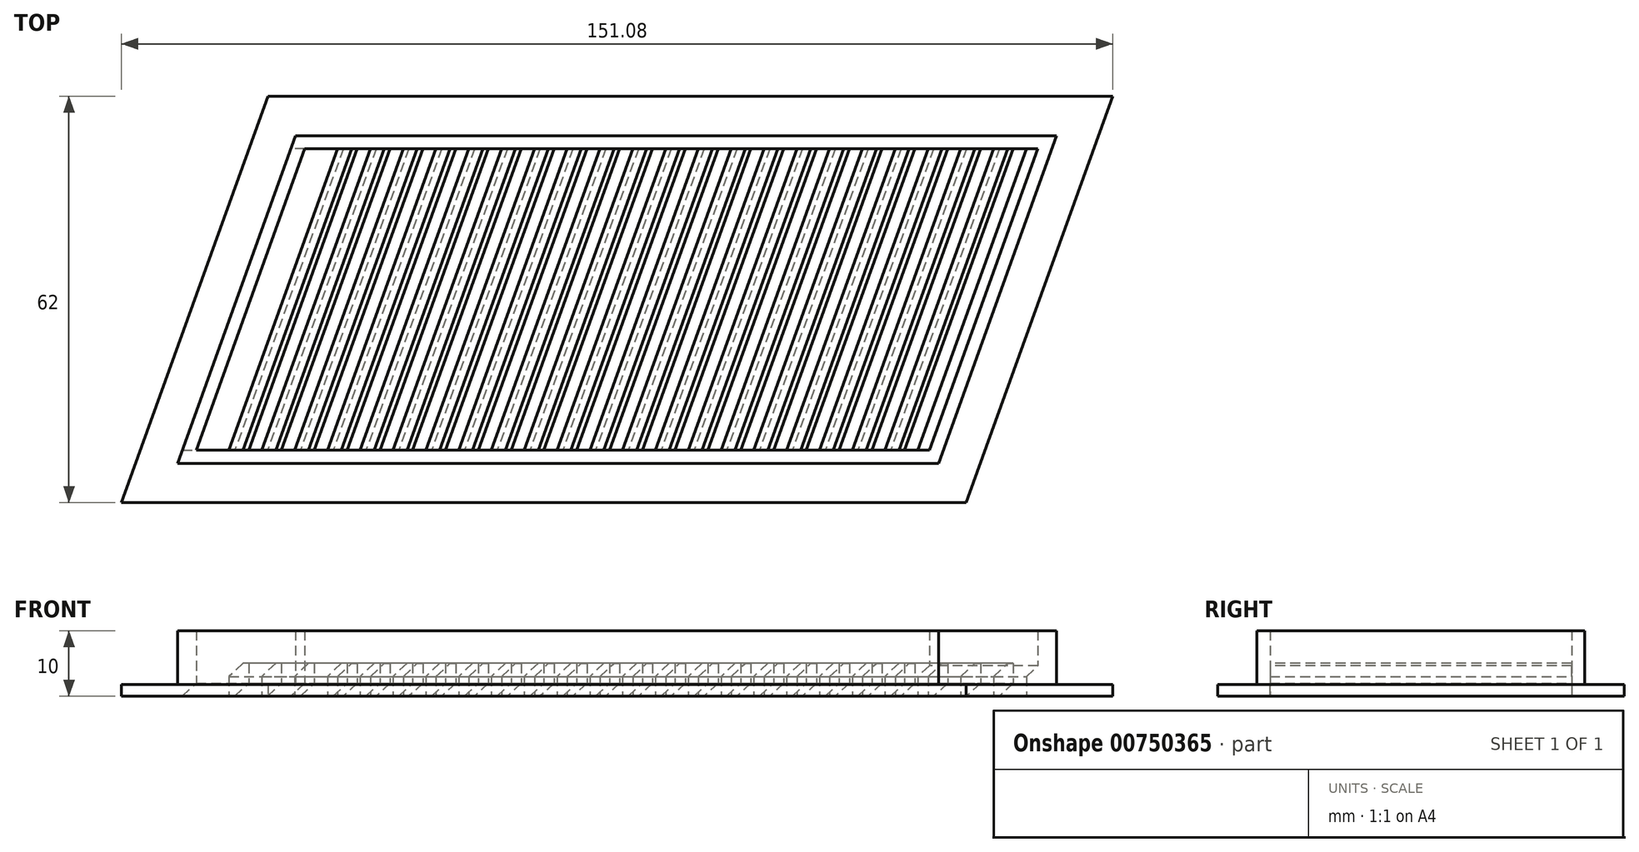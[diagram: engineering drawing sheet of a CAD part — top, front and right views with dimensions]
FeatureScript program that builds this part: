
annotation { "Feature Type Name" : "Feature", "Feature Type Description" : "" }
export const myFeature = defineFeature(function(context is Context, id is Id, definition is map)
    precondition{}
    {
        {
            var Q0;
            Q0=qCreatedBy(makeId("Top.planeOp"),FACE);
            var sketch = newSketch(context, id + "F0", { "sketchPlane" : qUnion([Q0])});
            skLineSegment(sketch, "E0", {"start": v(-116, 0) * mm, "end": v(0, 0) * mm});
            skLineSegment(sketch, "E1", {"start": v(-116, 0) * mm, "end": v(-98, 0) * mm});
            skLineSegment(sketch, "E2", {"start": v(-98, 0) * mm, "end": v(-98, 50) * mm, "construction": true});
            skLineSegment(sketch, "E3", {"start": v(18, 50) * mm, "end": v(-98, 50) * mm});
            skLineSegment(sketch, "E4", {"start": v(-98, 50) * mm, "end": v(-116, 0) * mm});
            skLineSegment(sketch, "E5", {"start": v(18, 50) * mm, "end": v(0, 0) * mm});
            skLineSegment(sketch, "E6.0", {"start": v(26.54, 56) * mm, "end": v(-102.22, 56) * mm});
            skLineSegment(sketch, "E6.1", {"start": v(26.54, 56) * mm, "end": v(4.22, -6) * mm});
            skLineSegment(sketch, "E6.2", {"start": v(-124.54, -6) * mm, "end": v(4.22, -6) * mm});
            skLineSegment(sketch, "E6.3", {"start": v(-102.22, 56) * mm, "end": v(-124.54, -6) * mm});
            skLineSegment(sketch, "E7.0", {"start": v(15.15, 48) * mm, "end": v(-96.6, 48) * mm});
            skLineSegment(sketch, "E7.1", {"start": v(15.15, 48) * mm, "end": v(-1.4, 2) * mm});
            skLineSegment(sketch, "E7.2", {"start": v(-113.15, 2) * mm, "end": v(-1.4, 2) * mm});
            skLineSegment(sketch, "E7.3", {"start": v(-96.6, 48) * mm, "end": v(-113.15, 2) * mm});
            skLineSegment(sketch, "E8.1.0.0", {"start": v(-91.6, 48) * mm, "end": v(-108.15, 2) * mm});
            skLineSegment(sketch, "E8.direction1", {"start": v(-113.15, 2) * mm, "end": v(-108.15, 2) * mm, "construction": true});
            skLineSegment(sketch, "E9.1.0.0", {"start": v(-88.6, 48) * mm, "end": v(-105.15, 2) * mm});
            skLineSegment(sketch, "E9.direction1", {"start": v(-113.15, 2) * mm, "end": v(-105.15, 2) * mm, "construction": true});
            skLineSegment(sketch, "E10.1.0.0", {"start": v(-86.6, 48) * mm, "end": v(-103.15, 2) * mm});
            skLineSegment(sketch, "E10.1.0.1", {"start": v(-83.6, 48) * mm, "end": v(-100.15, 2) * mm});
            skLineSegment(sketch, "E10.2.0.0", {"start": v(-81.6, 48) * mm, "end": v(-98.15, 2) * mm});
            skLineSegment(sketch, "E10.2.0.1", {"start": v(-78.6, 48) * mm, "end": v(-95.15, 2) * mm});
            skLineSegment(sketch, "E10.3.0.0", {"start": v(-76.6, 48) * mm, "end": v(-93.15, 2) * mm});
            skLineSegment(sketch, "E10.3.0.1", {"start": v(-73.6, 48) * mm, "end": v(-90.15, 2) * mm});
            skLineSegment(sketch, "E10.4.0.0", {"start": v(-71.6, 48) * mm, "end": v(-88.15, 2) * mm});
            skLineSegment(sketch, "E10.4.0.1", {"start": v(-68.6, 48) * mm, "end": v(-85.15, 2) * mm});
            skLineSegment(sketch, "E10.5.0.0", {"start": v(-66.6, 48) * mm, "end": v(-83.15, 2) * mm});
            skLineSegment(sketch, "E10.5.0.1", {"start": v(-63.6, 48) * mm, "end": v(-80.15, 2) * mm});
            skLineSegment(sketch, "E10.6.0.0", {"start": v(-61.6, 48) * mm, "end": v(-78.15, 2) * mm});
            skLineSegment(sketch, "E10.6.0.1", {"start": v(-58.6, 48) * mm, "end": v(-75.15, 2) * mm});
            skLineSegment(sketch, "E10.7.0.0", {"start": v(-56.6, 48) * mm, "end": v(-73.15, 2) * mm});
            skLineSegment(sketch, "E10.7.0.1", {"start": v(-53.6, 48) * mm, "end": v(-70.15, 2) * mm});
            skLineSegment(sketch, "E10.8.0.0", {"start": v(-51.6, 48) * mm, "end": v(-68.15, 2) * mm});
            skLineSegment(sketch, "E10.8.0.1", {"start": v(-48.6, 48) * mm, "end": v(-65.15, 2) * mm});
            skLineSegment(sketch, "E10.9.0.0", {"start": v(-46.6, 48) * mm, "end": v(-63.15, 2) * mm});
            skLineSegment(sketch, "E10.9.0.1", {"start": v(-43.6, 48) * mm, "end": v(-60.15, 2) * mm});
            skLineSegment(sketch, "E10.direction1", {"start": v(-108.15, 2) * mm, "end": v(-103.15, 2) * mm, "construction": true});
            skLineSegment(sketch, "E11.0.10.0", {"start": v(-41.6, 48) * mm, "end": v(-58.15, 2) * mm});
            skLineSegment(sketch, "E11.3.10.0", {"start": v(-38.6, 48) * mm, "end": v(-55.15, 2) * mm});
            skLineSegment(sketch, "E11.0.11.0", {"start": v(-36.6, 48) * mm, "end": v(-53.15, 2) * mm});
            skLineSegment(sketch, "E11.3.11.0", {"start": v(-33.6, 48) * mm, "end": v(-50.15, 2) * mm});
            skLineSegment(sketch, "E11.0.12.0", {"start": v(-31.6, 48) * mm, "end": v(-48.15, 2) * mm});
            skLineSegment(sketch, "E11.3.12.0", {"start": v(-28.6, 48) * mm, "end": v(-45.15, 2) * mm});
            skLineSegment(sketch, "E11.0.13.0", {"start": v(-26.6, 48) * mm, "end": v(-43.15, 2) * mm});
            skLineSegment(sketch, "E11.3.13.0", {"start": v(-23.6, 48) * mm, "end": v(-40.15, 2) * mm});
            skLineSegment(sketch, "E11.0.14.0", {"start": v(-21.6, 48) * mm, "end": v(-38.15, 2) * mm});
            skLineSegment(sketch, "E11.3.14.0", {"start": v(-18.6, 48) * mm, "end": v(-35.15, 2) * mm});
            skLineSegment(sketch, "E11.0.15.0", {"start": v(-16.6, 48) * mm, "end": v(-33.15, 2) * mm});
            skLineSegment(sketch, "E11.3.15.0", {"start": v(-13.6, 48) * mm, "end": v(-30.15, 2) * mm});
            skLineSegment(sketch, "E11.0.16.0", {"start": v(-11.6, 48) * mm, "end": v(-28.15, 2) * mm});
            skLineSegment(sketch, "E11.3.16.0", {"start": v(-8.6, 48) * mm, "end": v(-25.15, 2) * mm});
            skLineSegment(sketch, "E11.0.17.0", {"start": v(-6.6, 48) * mm, "end": v(-23.15, 2) * mm});
            skLineSegment(sketch, "E11.3.17.0", {"start": v(-3.6, 48) * mm, "end": v(-20.15, 2) * mm});
            skLineSegment(sketch, "E11.0.18.0", {"start": v(-1.6, 48) * mm, "end": v(-18.15, 2) * mm});
            skLineSegment(sketch, "E11.3.18.0", {"start": v(1.4, 48) * mm, "end": v(-15.15, 2) * mm});
            skLineSegment(sketch, "E11.0.19.0", {"start": v(3.4, 48) * mm, "end": v(-13.15, 2) * mm});
            skLineSegment(sketch, "E11.3.19.0", {"start": v(6.4, 48) * mm, "end": v(-10.15, 2) * mm});
            skLineSegment(sketch, "E12.0.20.0", {"start": v(8.4, 48) * mm, "end": v(-8.15, 2) * mm});
            skLineSegment(sketch, "E12.3.20.0", {"start": v(11.4, 48) * mm, "end": v(-5.15, 2) * mm});
            skLineSegment(sketch, "E12.0.21.0", {"start": v(13.4, 48) * mm, "end": v(-3.15, 2) * mm});
            skSolve(sketch);
        }
        {
            var Q0;
            Q0=makeQuery(id+"F0.imprint","IMPRINT",FACE,{"disambiguationData":[TD([[makeQuery(id+"F0.imprint","IMPRINT",EDGE,{"derivedFrom":sQuery(id+"F0.wireOp",EDGE,"E0")}),-1.0]])]});
            var Q1;
            Q1 = qConstructionFilter(qBodyType(qCreatedBy(id + "F0" ,EDGE), BodyType.WIRE), ConstructionObject.NO);
            extrude(context, id + "F1", {"entities" : qUnion([Q0]), "surfaceEntities" : qUnion([Q1]), "depth" : 1.8 * mm, "offsetDistance" : 25 * mm});
        }
        {
            var Q0;
            Q0=makeQuery(id+"F0.imprint","IMPRINT",FACE,{"disambiguationData":[TD([[makeQuery(id+"F0.imprint","IMPRINT",EDGE,{"derivedFrom":sQuery(id+"F0.wireOp",EDGE,"E0")}),1.0]])]});
            var Q1;
            {var subQ0=sQuery(id+"F0.wireOp",EDGE,"E8.1.0.0");Q1=makeQuery(id+"F0.imprint","IMPRINT",FACE,{"disambiguationData":[TD([[makeQuery(id+"F0.imprint","IMPRINT",EDGE,{"derivedFrom":subQ0}),1.0]])]});}
            var Q2;
            {var subQ0=sQuery(id+"F0.wireOp",EDGE,"E10.1.0.0");Q2=makeQuery(id+"F0.imprint","IMPRINT",FACE,{"disambiguationData":[TD([[makeQuery(id+"F0.imprint","IMPRINT",EDGE,{"derivedFrom":subQ0}),1.0]])]});}
            var Q3;
            {var subQ0=sQuery(id+"F0.wireOp",EDGE,"E10.2.0.0");Q3=makeQuery(id+"F0.imprint","IMPRINT",FACE,{"disambiguationData":[TD([[makeQuery(id+"F0.imprint","IMPRINT",EDGE,{"derivedFrom":subQ0}),1.0]])]});}
            var Q4;
            {var subQ0=sQuery(id+"F0.wireOp",EDGE,"E10.3.0.0");Q4=makeQuery(id+"F0.imprint","IMPRINT",FACE,{"disambiguationData":[TD([[makeQuery(id+"F0.imprint","IMPRINT",EDGE,{"derivedFrom":subQ0}),1.0]])]});}
            var Q5;
            {var subQ0=sQuery(id+"F0.wireOp",EDGE,"E10.4.0.0");Q5=makeQuery(id+"F0.imprint","IMPRINT",FACE,{"disambiguationData":[TD([[makeQuery(id+"F0.imprint","IMPRINT",EDGE,{"derivedFrom":subQ0}),1.0]])]});}
            var Q6;
            {var subQ0=sQuery(id+"F0.wireOp",EDGE,"E10.5.0.0");Q6=makeQuery(id+"F0.imprint","IMPRINT",FACE,{"disambiguationData":[TD([[makeQuery(id+"F0.imprint","IMPRINT",EDGE,{"derivedFrom":subQ0}),1.0]])]});}
            var Q7;
            {var subQ0=sQuery(id+"F0.wireOp",EDGE,"E10.6.0.0");Q7=makeQuery(id+"F0.imprint","IMPRINT",FACE,{"disambiguationData":[TD([[makeQuery(id+"F0.imprint","IMPRINT",EDGE,{"derivedFrom":subQ0}),1.0]])]});}
            var Q8;
            {var subQ0=sQuery(id+"F0.wireOp",EDGE,"E10.7.0.0");Q8=makeQuery(id+"F0.imprint","IMPRINT",FACE,{"disambiguationData":[TD([[makeQuery(id+"F0.imprint","IMPRINT",EDGE,{"derivedFrom":subQ0}),1.0]])]});}
            var Q9;
            {var subQ0=sQuery(id+"F0.wireOp",EDGE,"E10.8.0.0");Q9=makeQuery(id+"F0.imprint","IMPRINT",FACE,{"disambiguationData":[TD([[makeQuery(id+"F0.imprint","IMPRINT",EDGE,{"derivedFrom":subQ0}),1.0]])]});}
            var Q10;
            {var subQ0=sQuery(id+"F0.wireOp",EDGE,"E10.9.0.0");Q10=makeQuery(id+"F0.imprint","IMPRINT",FACE,{"disambiguationData":[TD([[makeQuery(id+"F0.imprint","IMPRINT",EDGE,{"derivedFrom":subQ0}),1.0]])]});}
            var Q11;
            {var subQ0=sQuery(id+"F0.wireOp",EDGE,"E11.0.10.0");Q11=makeQuery(id+"F0.imprint","IMPRINT",FACE,{"disambiguationData":[TD([[makeQuery(id+"F0.imprint","IMPRINT",EDGE,{"derivedFrom":subQ0}),1.0]])]});}
            var Q12;
            {var subQ0=sQuery(id+"F0.wireOp",EDGE,"E11.0.11.0");Q12=makeQuery(id+"F0.imprint","IMPRINT",FACE,{"disambiguationData":[TD([[makeQuery(id+"F0.imprint","IMPRINT",EDGE,{"derivedFrom":subQ0}),1.0]])]});}
            var Q13;
            {var subQ0=sQuery(id+"F0.wireOp",EDGE,"E11.0.12.0");Q13=makeQuery(id+"F0.imprint","IMPRINT",FACE,{"disambiguationData":[TD([[makeQuery(id+"F0.imprint","IMPRINT",EDGE,{"derivedFrom":subQ0}),1.0]])]});}
            var Q14;
            {var subQ0=sQuery(id+"F0.wireOp",EDGE,"E11.0.13.0");Q14=makeQuery(id+"F0.imprint","IMPRINT",FACE,{"disambiguationData":[TD([[makeQuery(id+"F0.imprint","IMPRINT",EDGE,{"derivedFrom":subQ0}),1.0]])]});}
            var Q15;
            {var subQ0=sQuery(id+"F0.wireOp",EDGE,"E11.0.14.0");Q15=makeQuery(id+"F0.imprint","IMPRINT",FACE,{"disambiguationData":[TD([[makeQuery(id+"F0.imprint","IMPRINT",EDGE,{"derivedFrom":subQ0}),1.0]])]});}
            var Q16;
            {var subQ0=sQuery(id+"F0.wireOp",EDGE,"E11.0.15.0");Q16=makeQuery(id+"F0.imprint","IMPRINT",FACE,{"disambiguationData":[TD([[makeQuery(id+"F0.imprint","IMPRINT",EDGE,{"derivedFrom":subQ0}),1.0]])]});}
            var Q17;
            {var subQ0=sQuery(id+"F0.wireOp",EDGE,"E11.0.16.0");Q17=makeQuery(id+"F0.imprint","IMPRINT",FACE,{"disambiguationData":[TD([[makeQuery(id+"F0.imprint","IMPRINT",EDGE,{"derivedFrom":subQ0}),1.0]])]});}
            var Q18;
            {var subQ0=sQuery(id+"F0.wireOp",EDGE,"E11.0.17.0");Q18=makeQuery(id+"F0.imprint","IMPRINT",FACE,{"disambiguationData":[TD([[makeQuery(id+"F0.imprint","IMPRINT",EDGE,{"derivedFrom":subQ0}),1.0]])]});}
            var Q19;
            {var subQ0=sQuery(id+"F0.wireOp",EDGE,"E11.0.18.0");Q19=makeQuery(id+"F0.imprint","IMPRINT",FACE,{"disambiguationData":[TD([[makeQuery(id+"F0.imprint","IMPRINT",EDGE,{"derivedFrom":subQ0}),1.0]])]});}
            var Q20;
            {var subQ0=sQuery(id+"F0.wireOp",EDGE,"E11.0.19.0");Q20=makeQuery(id+"F0.imprint","IMPRINT",FACE,{"disambiguationData":[TD([[makeQuery(id+"F0.imprint","IMPRINT",EDGE,{"derivedFrom":subQ0}),1.0]])]});}
            var Q21;
            {var subQ0=sQuery(id+"F0.wireOp",EDGE,"E12.0.20.0");Q21=makeQuery(id+"F0.imprint","IMPRINT",FACE,{"disambiguationData":[TD([[makeQuery(id+"F0.imprint","IMPRINT",EDGE,{"derivedFrom":subQ0}),1.0]])]});}
            var Q22;
            {var subQ0=sQuery(id+"F0.wireOp",EDGE,"E12.0.21.0");Q22=makeQuery(id+"F0.imprint","IMPRINT",FACE,{"disambiguationData":[TD([[makeQuery(id+"F0.imprint","IMPRINT",EDGE,{"derivedFrom":subQ0}),1.0]])]});}
            extrude(context, id + "F2", {"entities" : qUnion([Q0, Q1, Q2, Q3, Q4, Q5, Q6, Q7, Q8, Q9, Q10, Q11, Q12, Q13, Q14, Q15, Q16, Q17, Q18, Q19, Q20, Q21, Q22]), "depth" : 5 * mm, "offsetDistance" : 25 * mm});
        }
        {
            var Q0;
            Q0=makeQuery(id+"F0.imprint","IMPRINT",FACE,{"disambiguationData":[TD([[makeQuery(id+"F0.imprint","IMPRINT",EDGE,{"derivedFrom":sQuery(id+"F0.wireOp",EDGE,"E0")}),1.0]])]});
            extrude(context, id + "F3", {"entities" : qUnion([Q0]), "operationType" : NewBodyOperationType.ADD, "depth" : 10 * mm, "offsetDistance" : 25 * mm});
        }
        {
            var Q0;
            Q0=makeQuery(id+"F2.opExtrude","CAP_EDGE",EDGE,{"disambiguationData":[OSD([sQuery(id+"F0.wireOp",EDGE,"E10.9.0.1")])],"isStart":true});
            var Q1;
            Q1=makeQuery(id+"F2.opExtrude","CAP_EDGE",EDGE,{"disambiguationData":[OSD([sQuery(id+"F0.wireOp",EDGE,"E10.8.0.1")])],"isStart":true});
            var Q2;
            Q2=makeQuery(id+"F2.opExtrude","CAP_EDGE",EDGE,{"disambiguationData":[OSD([sQuery(id+"F0.wireOp",EDGE,"E10.7.0.1")])],"isStart":true});
            var Q3;
            Q3=makeQuery(id+"F2.opExtrude","CAP_EDGE",EDGE,{"disambiguationData":[OSD([sQuery(id+"F0.wireOp",EDGE,"E10.6.0.1")])],"isStart":true});
            var Q4;
            Q4=makeQuery(id+"F2.opExtrude","CAP_EDGE",EDGE,{"disambiguationData":[OSD([sQuery(id+"F0.wireOp",EDGE,"E10.5.0.1")])],"isStart":true});
            var Q5;
            Q5=makeQuery(id+"F2.opExtrude","CAP_EDGE",EDGE,{"disambiguationData":[OSD([sQuery(id+"F0.wireOp",EDGE,"E10.4.0.1")])],"isStart":true});
            var Q6;
            Q6=makeQuery(id+"F2.opExtrude","CAP_EDGE",EDGE,{"disambiguationData":[OSD([sQuery(id+"F0.wireOp",EDGE,"E10.3.0.1")])],"isStart":true});
            var Q7;
            Q7=makeQuery(id+"F2.opExtrude","CAP_EDGE",EDGE,{"disambiguationData":[OSD([sQuery(id+"F0.wireOp",EDGE,"E10.2.0.1")])],"isStart":true});
            var Q8;
            Q8=makeQuery(id+"F2.opExtrude","CAP_EDGE",EDGE,{"disambiguationData":[OSD([sQuery(id+"F0.wireOp",EDGE,"E10.1.0.1")])],"isStart":true});
            var Q9;
            Q9=makeQuery(id+"F2.opExtrude","CAP_EDGE",EDGE,{"disambiguationData":[OSD([sQuery(id+"F0.wireOp",EDGE,"E9.1.0.0")])],"isStart":true});
            var Q10;
            Q10=makeQuery(id+"F2.opExtrude","CAP_EDGE",EDGE,{"disambiguationData":[OSD([sQuery(id+"F0.wireOp",EDGE,"E10.9.0.0")])],"isStart":false});
            var Q11;
            Q11=makeQuery(id+"F2.opExtrude","CAP_EDGE",EDGE,{"disambiguationData":[OSD([sQuery(id+"F0.wireOp",EDGE,"E10.8.0.0")])],"isStart":false});
            var Q12;
            Q12=makeQuery(id+"F2.opExtrude","CAP_EDGE",EDGE,{"disambiguationData":[OSD([sQuery(id+"F0.wireOp",EDGE,"E10.7.0.0")])],"isStart":false});
            var Q13;
            Q13=makeQuery(id+"F2.opExtrude","CAP_EDGE",EDGE,{"disambiguationData":[OSD([sQuery(id+"F0.wireOp",EDGE,"E10.6.0.0")])],"isStart":false});
            var Q14;
            Q14=makeQuery(id+"F2.opExtrude","CAP_EDGE",EDGE,{"disambiguationData":[OSD([sQuery(id+"F0.wireOp",EDGE,"E10.5.0.0")])],"isStart":false});
            var Q15;
            Q15=makeQuery(id+"F2.opExtrude","CAP_EDGE",EDGE,{"disambiguationData":[OSD([sQuery(id+"F0.wireOp",EDGE,"E10.4.0.0")])],"isStart":false});
            var Q16;
            Q16=makeQuery(id+"F2.opExtrude","CAP_EDGE",EDGE,{"disambiguationData":[OSD([sQuery(id+"F0.wireOp",EDGE,"E10.3.0.0")])],"isStart":false});
            var Q17;
            Q17=makeQuery(id+"F2.opExtrude","CAP_EDGE",EDGE,{"disambiguationData":[OSD([sQuery(id+"F0.wireOp",EDGE,"E10.2.0.0")])],"isStart":false});
            var Q18;
            Q18=makeQuery(id+"F2.opExtrude","CAP_EDGE",EDGE,{"disambiguationData":[OSD([sQuery(id+"F0.wireOp",EDGE,"E10.1.0.0")])],"isStart":false});
            var Q19;
            Q19=makeQuery(id+"F2.opExtrude","CAP_EDGE",EDGE,{"disambiguationData":[OSD([sQuery(id+"F0.wireOp",EDGE,"E8.1.0.0")])],"isStart":false});
            var Q20;
            Q20=makeQuery(id+"F2.opExtrude","CAP_EDGE",EDGE,{"disambiguationData":[OSD([sQuery(id+"F0.wireOp",EDGE,"E11.3.10.0")])],"isStart":true});
            var Q21;
            Q21=makeQuery(id+"F2.opExtrude","CAP_EDGE",EDGE,{"disambiguationData":[OSD([sQuery(id+"F0.wireOp",EDGE,"E11.3.11.0")])],"isStart":true});
            var Q22;
            Q22=makeQuery(id+"F2.opExtrude","CAP_EDGE",EDGE,{"disambiguationData":[OSD([sQuery(id+"F0.wireOp",EDGE,"E11.3.12.0")])],"isStart":true});
            var Q23;
            Q23=makeQuery(id+"F2.opExtrude","CAP_EDGE",EDGE,{"disambiguationData":[OSD([sQuery(id+"F0.wireOp",EDGE,"E11.3.13.0")])],"isStart":true});
            var Q24;
            Q24=makeQuery(id+"F2.opExtrude","CAP_EDGE",EDGE,{"disambiguationData":[OSD([sQuery(id+"F0.wireOp",EDGE,"E11.3.14.0")])],"isStart":true});
            var Q25;
            Q25=makeQuery(id+"F2.opExtrude","CAP_EDGE",EDGE,{"disambiguationData":[OSD([sQuery(id+"F0.wireOp",EDGE,"E11.3.15.0")])],"isStart":true});
            var Q26;
            Q26=makeQuery(id+"F2.opExtrude","CAP_EDGE",EDGE,{"disambiguationData":[OSD([sQuery(id+"F0.wireOp",EDGE,"E11.3.16.0")])],"isStart":true});
            var Q27;
            Q27=makeQuery(id+"F2.opExtrude","CAP_EDGE",EDGE,{"disambiguationData":[OSD([sQuery(id+"F0.wireOp",EDGE,"E11.3.17.0")])],"isStart":true});
            var Q28;
            Q28=makeQuery(id+"F2.opExtrude","CAP_EDGE",EDGE,{"disambiguationData":[OSD([sQuery(id+"F0.wireOp",EDGE,"E11.3.18.0")])],"isStart":true});
            var Q29;
            Q29=makeQuery(id+"F2.opExtrude","CAP_EDGE",EDGE,{"disambiguationData":[OSD([sQuery(id+"F0.wireOp",EDGE,"E11.3.19.0")])],"isStart":true});
            var Q30;
            Q30=makeQuery(id+"F2.opExtrude","CAP_EDGE",EDGE,{"disambiguationData":[OSD([sQuery(id+"F0.wireOp",EDGE,"E12.3.20.0")])],"isStart":true});
            var Q31;
            Q31=makeQuery(id+"F2.opExtrude","CAP_EDGE",EDGE,{"disambiguationData":[OSD([sQuery(id+"F0.wireOp",EDGE,"E12.3.21.0")])],"isStart":true});
            var Q32;
            Q32=makeQuery(id+"F2.opExtrude","CAP_EDGE",EDGE,{"disambiguationData":[OSD([sQuery(id+"F0.wireOp",EDGE,"E11.0.10.0")])],"isStart":false});
            var Q33;
            Q33=makeQuery(id+"F2.opExtrude","CAP_EDGE",EDGE,{"disambiguationData":[OSD([sQuery(id+"F0.wireOp",EDGE,"E11.0.11.0")])],"isStart":false});
            var Q34;
            Q34=makeQuery(id+"F2.opExtrude","CAP_EDGE",EDGE,{"disambiguationData":[OSD([sQuery(id+"F0.wireOp",EDGE,"E11.0.12.0")])],"isStart":false});
            var Q35;
            Q35=makeQuery(id+"F2.opExtrude","CAP_EDGE",EDGE,{"disambiguationData":[OSD([sQuery(id+"F0.wireOp",EDGE,"E11.0.13.0")])],"isStart":false});
            var Q36;
            Q36=makeQuery(id+"F2.opExtrude","CAP_EDGE",EDGE,{"disambiguationData":[OSD([sQuery(id+"F0.wireOp",EDGE,"E11.0.14.0")])],"isStart":false});
            var Q37;
            Q37=makeQuery(id+"F2.opExtrude","CAP_EDGE",EDGE,{"disambiguationData":[OSD([sQuery(id+"F0.wireOp",EDGE,"E11.0.15.0")])],"isStart":false});
            var Q38;
            Q38=makeQuery(id+"F2.opExtrude","CAP_EDGE",EDGE,{"disambiguationData":[OSD([sQuery(id+"F0.wireOp",EDGE,"E11.0.16.0")])],"isStart":false});
            var Q39;
            Q39=makeQuery(id+"F2.opExtrude","CAP_EDGE",EDGE,{"disambiguationData":[OSD([sQuery(id+"F0.wireOp",EDGE,"E11.0.17.0")])],"isStart":false});
            var Q40;
            Q40=makeQuery(id+"F2.opExtrude","CAP_EDGE",EDGE,{"disambiguationData":[OSD([sQuery(id+"F0.wireOp",EDGE,"E11.0.18.0")])],"isStart":false});
            var Q41;
            Q41=makeQuery(id+"F2.opExtrude","CAP_EDGE",EDGE,{"disambiguationData":[OSD([sQuery(id+"F0.wireOp",EDGE,"E11.0.19.0")])],"isStart":false});
            var Q42;
            Q42=makeQuery(id+"F2.opExtrude","CAP_EDGE",EDGE,{"disambiguationData":[OSD([sQuery(id+"F0.wireOp",EDGE,"E12.0.20.0")])],"isStart":false});
            var Q43;
            Q43=makeQuery(id+"F2.opExtrude","CAP_EDGE",EDGE,{"disambiguationData":[OSD([sQuery(id+"F0.wireOp",EDGE,"E12.0.21.0")])],"isStart":false});
            var Q44;
            Q44=makeQuery(id+"F2.opExtrude","CAP_EDGE",EDGE,{"disambiguationData":[OSD([sQuery(id+"F0.wireOp",EDGE,"E7.3")])],"isStart":true});
            chamfer(context, id + "F4", {"entities" : qUnion([Q0, Q1, Q2, Q3, Q4, Q5, Q6, Q7, Q8, Q9, Q10, Q11, Q12, Q13, Q14, Q15, Q16, Q17, Q18, Q19, Q20, Q21, Q22, Q23, Q24, Q25, Q26, Q27, Q28, Q29, Q30, Q31, Q32, Q33, Q34, Q35, Q36, Q37, Q38, Q39, Q40, Q41, Q42, Q43, Q44]), "width" : 2 * mm, "tangentPropagation" : true});
        }
    });
